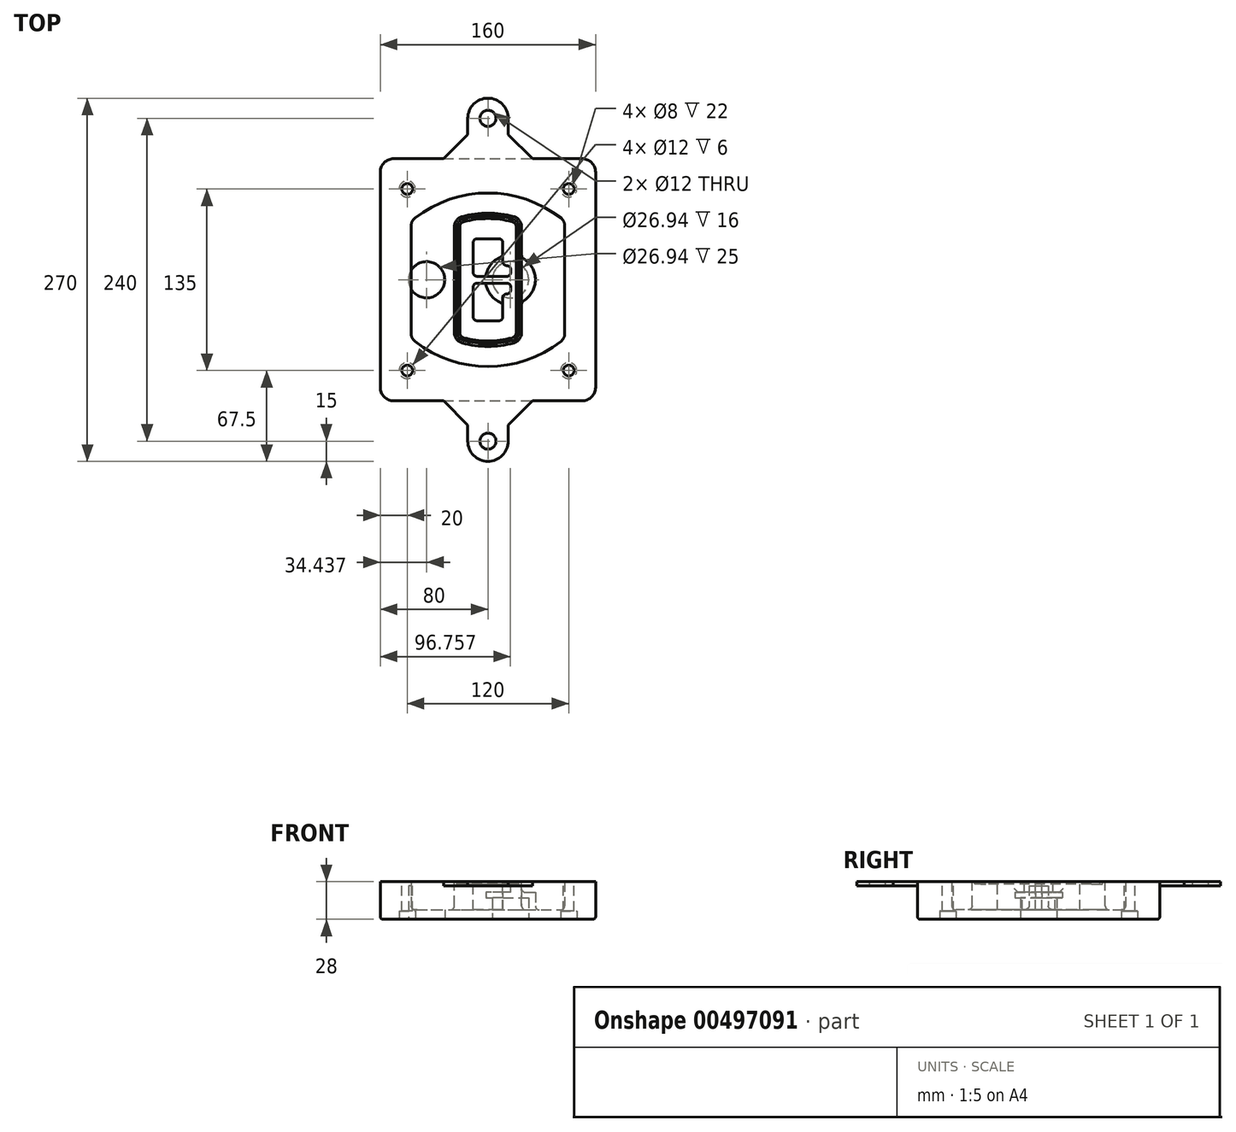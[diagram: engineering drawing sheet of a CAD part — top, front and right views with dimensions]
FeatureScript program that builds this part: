
annotation { "Feature Type Name" : "Feature", "Feature Type Description" : "" }
export const myFeature = defineFeature(function(context is Context, id is Id, definition is map)
    precondition{}
    {
        {
            var Q0;
            Q0=qCreatedBy(makeId("Top.planeOp"),FACE);
            var sketch = newSketch(context, id + "F0", { "sketchPlane" : qUnion([Q0])});
            skPoint(sketch, "E0.rect.middle", {"position": v(0, 0) * mm});
            skLineSegment(sketch, "E1.bottom", {"start": v(-70, -90) * mm, "end": v(70, -90) * mm});
            skLineSegment(sketch, "E1.top", {"start": v(-70, 90) * mm, "end": v(70, 90) * mm});
            skLineSegment(sketch, "E1.left", {"start": v(-80, -80) * mm, "end": v(-80, 80) * mm});
            skLineSegment(sketch, "E1.right", {"start": v(80, -80) * mm, "end": v(80, 80) * mm});
            skLineSegment(sketch, "E2", {"start": v(-80, 90) * mm, "end": v(80, -90) * mm, "construction": true});
            skLineSegment(sketch, "E3", {"start": v(80, 90) * mm, "end": v(-80, -90) * mm, "construction": true});
            skCircle(sketch, "E4", {"center": v(-60, 67.5) * mm, "radius": 4 * mm});
            skCircle(sketch, "E5", {"center": v(60, 67.5) * mm, "radius": 4 * mm});
            skCircle(sketch, "E6", {"center": v(60, -67.5) * mm, "radius": 4 * mm});
            skCircle(sketch, "E7", {"center": v(-60, -67.5) * mm, "radius": 4 * mm});
            skLineSegment(sketch, "E8", {"start": v(-60, 67.5) * mm, "end": v(60, 67.5) * mm, "construction": true});
            skLineSegment(sketch, "E9", {"start": v(60, 67.5) * mm, "end": v(60, -67.5) * mm, "construction": true});
            skLineSegment(sketch, "E10", {"start": v(60, -67.5) * mm, "end": v(-60, -67.5) * mm, "construction": true});
            skLineSegment(sketch, "E11", {"start": v(-60, -67.5) * mm, "end": v(-60, 67.5) * mm, "construction": true});
            skLineSegment(sketch, "E12", {"start": v(-60, 40.3) * mm, "end": v(-60, -40.3) * mm});
            skLineSegment(sketch, "E13", {"start": v(60, 40.3) * mm, "end": v(60, -40.3) * mm});
            skArc(sketch, "E14", {"start": v(56.15, 48.18) * mm, "mid": v(0, 67.5) * mm, "end": v(-56.15, 48.18) * mm});
            skArc(sketch, "E15", {"start": v(-56.15, -48.18) * mm, "mid": v(0, -67.5) * mm, "end": v(56.15, -48.18) * mm});
            skLineSegment(sketch, "E16", {"start": v(-60, 0) * mm, "end": v(60, 0) * mm, "construction": true});
            skPoint(sketch, "E17.visualSharp", {"position": v(-60, -45) * mm});
            skArc(sketch, "E17.filletArc", {"start": v(-60, -40.3) * mm, "mid": v(-58.99, -44.68) * mm, "end": v(-56.15, -48.18) * mm});
            skPoint(sketch, "E18.visualSharp", {"position": v(-60, 45) * mm});
            skArc(sketch, "E18.filletArc", {"start": v(-56.15, 48.18) * mm, "mid": v(-58.99, 44.68) * mm, "end": v(-60, 40.3) * mm});
            skPoint(sketch, "E19.visualSharp", {"position": v(60, 45) * mm});
            skArc(sketch, "E19.filletArc", {"start": v(60, 40.3) * mm, "mid": v(58.99, 44.68) * mm, "end": v(56.15, 48.18) * mm});
            skPoint(sketch, "E20.visualSharp", {"position": v(60, -45) * mm});
            skArc(sketch, "E20.filletArc", {"start": v(56.15, -48.18) * mm, "mid": v(58.99, -44.68) * mm, "end": v(60, -40.3) * mm});
            skPoint(sketch, "E21.visualSharp", {"position": v(-80, 90) * mm});
            skArc(sketch, "E21.filletArc", {"start": v(-70, 90) * mm, "mid": v(-77.07, 87.07) * mm, "end": v(-80, 80) * mm});
            skPoint(sketch, "E22.visualSharp", {"position": v(80, 90) * mm});
            skArc(sketch, "E22.filletArc", {"start": v(80, 80) * mm, "mid": v(77.07, 87.07) * mm, "end": v(70, 90) * mm});
            skPoint(sketch, "E23.visualSharp", {"position": v(80, -90) * mm});
            skArc(sketch, "E23.filletArc", {"start": v(70, -90) * mm, "mid": v(77.07, -87.07) * mm, "end": v(80, -80) * mm});
            skPoint(sketch, "E24.visualSharp", {"position": v(-80, -90) * mm});
            skArc(sketch, "E24.filletArc", {"start": v(-80, -80) * mm, "mid": v(-77.07, -87.07) * mm, "end": v(-70, -90) * mm});
            skArc(sketch, "E25.0", {"start": v(57, 40.3) * mm, "mid": v(56.3, 43.36) * mm, "end": v(54.3, 45.81) * mm});
            skLineSegment(sketch, "E25.1", {"start": v(57, 40.3) * mm, "end": v(57, -40.3) * mm});
            skArc(sketch, "E25.2", {"start": v(54.3, -45.81) * mm, "mid": v(56.3, -43.36) * mm, "end": v(57, -40.3) * mm});
            skArc(sketch, "E25.3", {"start": v(-54.3, -45.81) * mm, "mid": v(0, -64.5) * mm, "end": v(54.3, -45.81) * mm});
            skArc(sketch, "E25.4", {"start": v(-57, -40.3) * mm, "mid": v(-56.3, -43.36) * mm, "end": v(-54.3, -45.81) * mm});
            skArc(sketch, "E25.5", {"start": v(54.3, 45.81) * mm, "mid": v(0, 64.5) * mm, "end": v(-54.3, 45.81) * mm});
            skLineSegment(sketch, "E25.6", {"start": v(-57, 40.3) * mm, "end": v(-57, -40.3) * mm});
            skArc(sketch, "E25.7", {"start": v(-54.3, 45.81) * mm, "mid": v(-56.3, 43.36) * mm, "end": v(-57, 40.3) * mm});
            skArc(sketch, "E26.0", {"start": v(-58.62, 51.33) * mm, "mid": v(-62.58, 46.43) * mm, "end": v(-64, 40.3) * mm});
            skArc(sketch, "E26.1", {"start": v(58.62, 51.33) * mm, "mid": v(0, 71.5) * mm, "end": v(-58.62, 51.33) * mm});
            skArc(sketch, "E26.2", {"start": v(64, 40.3) * mm, "mid": v(62.58, 46.43) * mm, "end": v(58.62, 51.33) * mm});
            skLineSegment(sketch, "E26.3", {"start": v(64, 40.3) * mm, "end": v(64, -40.3) * mm});
            skArc(sketch, "E26.4", {"start": v(58.62, -51.33) * mm, "mid": v(62.58, -46.43) * mm, "end": v(64, -40.3) * mm});
            skLineSegment(sketch, "E26.5", {"start": v(-64, 40.3) * mm, "end": v(-64, -40.3) * mm});
            skArc(sketch, "E26.6", {"start": v(-58.62, -51.33) * mm, "mid": v(0, -71.5) * mm, "end": v(58.62, -51.33) * mm});
            skArc(sketch, "E26.7", {"start": v(-64, -40.3) * mm, "mid": v(-62.58, -46.43) * mm, "end": v(-58.62, -51.33) * mm});
            skSolve(sketch);
        }
        {
            var Q0;
            Q0=makeQuery(id+"F0.imprint","IMPRINT",FACE,{"disambiguationData":[TD([[makeQuery(id+"F0.imprint","IMPRINT",EDGE,{"derivedFrom":sQuery(id+"F0.wireOp",EDGE,"E1.bottom")}),1.0]])]});
            var Q1;
            Q1=makeQuery(id+"F0.imprint","IMPRINT",FACE,{"disambiguationData":[TD([[makeQuery(id+"F0.imprint","IMPRINT",EDGE,{"derivedFrom":sQuery(id+"F0.wireOp",EDGE,"E12")}),1.0]])]});
            var Q2;
            Q2=makeQuery(id+"F0.imprint","IMPRINT",FACE,{"disambiguationData":[TD([[makeQuery(id+"F0.imprint","IMPRINT",EDGE,{"derivedFrom":sQuery(id+"F0.wireOp",EDGE,"E25.0")}),1.0]])]});
            var Q3;
            Q3=makeQuery(id+"F0.imprint","IMPRINT",FACE,{"disambiguationData":[TD([[makeQuery(id+"F0.imprint","IMPRINT",EDGE,{"derivedFrom":sQuery(id+"F0.wireOp",EDGE,"E12")}),-1.0]])]});
            extrude(context, id + "F1", {"entities" : qUnion([Q0, Q1, Q2, Q3]), "oppositeDirection" : true, "depth" : 25 * mm});
        }
        {
            var Q0;
            Q0=makeQuery(id+"F0.imprint","IMPRINT",FACE,{"disambiguationData":[TD([[makeQuery(id+"F0.imprint","IMPRINT",EDGE,{"derivedFrom":sQuery(id+"F0.wireOp",EDGE,"E12")}),1.0]])]});
            extrude(context, id + "F2", {"entities" : qUnion([Q0]), "operationType" : NewBodyOperationType.ADD, "depth" : 3 * mm});
        }
        {
            var Q0;
            Q0=makeQuery(id+"F0.imprint","IMPRINT",FACE,{"disambiguationData":[TD([[makeQuery(id+"F0.imprint","IMPRINT",EDGE,{"derivedFrom":sQuery(id+"F0.wireOp",EDGE,"E25.0")}),1.0]])]});
            extrude(context, id + "F3", {"entities" : qUnion([Q0]), "operationType" : NewBodyOperationType.REMOVE, "oppositeDirection" : true, "depth" : 18 * mm});
        }
        {
            var Q0;
            Q0=makeQuery(id+"F2.opExtrude","CAP_FACE",FACE,{"disambiguationData":[OSD([sQuery(id+"F0.wireOp",EDGE,"E12"),sQuery(id+"F0.wireOp",EDGE,"E13"),sQuery(id+"F0.wireOp",EDGE,"E14"),sQuery(id+"F0.wireOp",EDGE,"E15"),sQuery(id+"F0.wireOp",EDGE,"E17.filletArc"),sQuery(id+"F0.wireOp",EDGE,"E18.filletArc"),sQuery(id+"F0.wireOp",EDGE,"E19.filletArc"),sQuery(id+"F0.wireOp",EDGE,"E20.filletArc"),sQuery(id+"F0.wireOp",EDGE,"E25.0"),sQuery(id+"F0.wireOp",EDGE,"E25.1"),sQuery(id+"F0.wireOp",EDGE,"E25.2"),sQuery(id+"F0.wireOp",EDGE,"E25.3"),sQuery(id+"F0.wireOp",EDGE,"E25.4"),sQuery(id+"F0.wireOp",EDGE,"E25.5"),sQuery(id+"F0.wireOp",EDGE,"E25.6"),sQuery(id+"F0.wireOp",EDGE,"E25.7")])],"isStart":false});
            var sketch = newSketch(context, id + "F4", { "sketchPlane" : qUnion([Q0])});
            skArc(sketch, "E27.0", {"start": v(-19.08, -46.97) * mm, "mid": v(0, -49.5) * mm, "end": v(19.08, -46.97) * mm});
            skArc(sketch, "E28.0", {"start": v(19.08, 46.97) * mm, "mid": v(0, 49.5) * mm, "end": v(-19.08, 46.97) * mm});
            skLineSegment(sketch, "E29", {"start": v(-25, 39.25) * mm, "end": v(-25, -39.25) * mm});
            skLineSegment(sketch, "E30", {"start": v(25, 39.25) * mm, "end": v(25, -39.25) * mm});
            skLineSegment(sketch, "E31", {"start": v(-25, 45.1) * mm, "end": v(25, 45.1) * mm, "construction": true});
            skLineSegment(sketch, "E32", {"start": v(-25, -45.1) * mm, "end": v(25, -45.1) * mm, "construction": true});
            skPoint(sketch, "E33.visualSharp", {"position": v(-25, 45.1) * mm});
            skArc(sketch, "E33.filletArc", {"start": v(-19.08, 46.97) * mm, "mid": v(-23.35, 44.11) * mm, "end": v(-25, 39.25) * mm});
            skPoint(sketch, "E34.visualSharp", {"position": v(25, 45.1) * mm});
            skArc(sketch, "E34.filletArc", {"start": v(25, 39.25) * mm, "mid": v(23.35, 44.11) * mm, "end": v(19.08, 46.97) * mm});
            skPoint(sketch, "E35.visualSharp", {"position": v(25, -45.1) * mm});
            skArc(sketch, "E35.filletArc", {"start": v(19.08, -46.97) * mm, "mid": v(23.35, -44.11) * mm, "end": v(25, -39.25) * mm});
            skPoint(sketch, "E36.visualSharp", {"position": v(-25, -45.1) * mm});
            skArc(sketch, "E36.filletArc", {"start": v(-25, -39.25) * mm, "mid": v(-23.35, -44.11) * mm, "end": v(-19.08, -46.97) * mm});
            skArc(sketch, "E37.0", {"start": v(54.3, 45.81) * mm, "mid": v(0, 64.5) * mm, "end": v(-54.3, 45.81) * mm});
            skArc(sketch, "E37.1", {"start": v(-54.3, 45.81) * mm, "mid": v(-56.3, 43.36) * mm, "end": v(-57, 40.3) * mm});
            skLineSegment(sketch, "E37.2", {"start": v(-57, 40.3) * mm, "end": v(-57, -40.3) * mm});
            skArc(sketch, "E37.3", {"start": v(-57, -40.3) * mm, "mid": v(-56.3, -43.36) * mm, "end": v(-54.3, -45.81) * mm});
            skArc(sketch, "E37.4", {"start": v(-54.3, -45.81) * mm, "mid": v(0, -64.5) * mm, "end": v(54.3, -45.81) * mm});
            skArc(sketch, "E37.5", {"start": v(54.3, -45.81) * mm, "mid": v(56.3, -43.36) * mm, "end": v(57, -40.3) * mm});
            skLineSegment(sketch, "E37.6", {"start": v(57, 40.3) * mm, "end": v(57, -40.3) * mm});
            skArc(sketch, "E37.7", {"start": v(57, 40.3) * mm, "mid": v(56.3, 43.36) * mm, "end": v(54.3, 45.81) * mm});
            skLineSegment(sketch, "E38.0", {"start": v(23, 39.25) * mm, "end": v(23, -39.25) * mm});
            skArc(sketch, "E38.1", {"start": v(18.56, -45.04) * mm, "mid": v(21.76, -42.9) * mm, "end": v(23, -39.25) * mm});
            skArc(sketch, "E38.2", {"start": v(-18.56, -45.04) * mm, "mid": v(0, -47.5) * mm, "end": v(18.56, -45.04) * mm});
            skArc(sketch, "E38.3", {"start": v(-23, -39.25) * mm, "mid": v(-21.76, -42.9) * mm, "end": v(-18.56, -45.04) * mm});
            skLineSegment(sketch, "E38.4", {"start": v(-23, 39.25) * mm, "end": v(-23, -39.25) * mm});
            skArc(sketch, "E38.5", {"start": v(23, 39.25) * mm, "mid": v(21.76, 42.9) * mm, "end": v(18.56, 45.04) * mm});
            skArc(sketch, "E38.6", {"start": v(-18.56, 45.04) * mm, "mid": v(-21.76, 42.9) * mm, "end": v(-23, 39.25) * mm});
            skArc(sketch, "E38.7", {"start": v(18.56, 45.04) * mm, "mid": v(0, 47.5) * mm, "end": v(-18.56, 45.04) * mm});
            skArc(sketch, "E39.0", {"start": v(21, 39.25) * mm, "mid": v(20.18, 41.68) * mm, "end": v(18.04, 43.1) * mm});
            skLineSegment(sketch, "E39.1", {"start": v(21, 39.25) * mm, "end": v(21, -39.25) * mm});
            skArc(sketch, "E39.2", {"start": v(18.04, -43.1) * mm, "mid": v(20.18, -41.68) * mm, "end": v(21, -39.25) * mm});
            skArc(sketch, "E39.3", {"start": v(-18.04, -43.1) * mm, "mid": v(0, -45.5) * mm, "end": v(18.04, -43.1) * mm});
            skArc(sketch, "E39.4", {"start": v(-21, -39.25) * mm, "mid": v(-20.18, -41.68) * mm, "end": v(-18.04, -43.1) * mm});
            skArc(sketch, "E39.5", {"start": v(18.04, 43.1) * mm, "mid": v(0, 45.5) * mm, "end": v(-18.04, 43.1) * mm});
            skLineSegment(sketch, "E39.6", {"start": v(-21, 39.25) * mm, "end": v(-21, -39.25) * mm});
            skArc(sketch, "E39.7", {"start": v(-18.04, 43.1) * mm, "mid": v(-20.18, 41.68) * mm, "end": v(-21, 39.25) * mm});
            skLineSegment(sketch, "E40", {"start": v(-25, 0) * mm, "end": v(25, 0) * mm, "construction": true});
            skLineSegment(sketch, "E41", {"start": v(-11, 5.5) * mm, "end": v(-11, 27.5) * mm});
            skLineSegment(sketch, "E42", {"start": v(-8, 30.5) * mm, "end": v(8, 30.5) * mm});
            skLineSegment(sketch, "E43", {"start": v(11, 27.5) * mm, "end": v(11, 13.5) * mm});
            skLineSegment(sketch, "E44", {"start": v(14, 10.5) * mm, "end": v(14, 10.5) * mm});
            skLineSegment(sketch, "E45", {"start": v(17, 7.5) * mm, "end": v(17, 5.5) * mm});
            skLineSegment(sketch, "E46", {"start": v(14, 2.5) * mm, "end": v(-8, 2.5) * mm});
            skPoint(sketch, "E47.visualSharp", {"position": v(-11, 30.5) * mm});
            skArc(sketch, "E47.filletArc", {"start": v(-8, 30.5) * mm, "mid": v(-10.12, 29.62) * mm, "end": v(-11, 27.5) * mm});
            skPoint(sketch, "E48.visualSharp", {"position": v(11, 30.5) * mm});
            skArc(sketch, "E48.filletArc", {"start": v(11, 27.5) * mm, "mid": v(10.12, 29.62) * mm, "end": v(8, 30.5) * mm});
            skPoint(sketch, "E49.visualSharp", {"position": v(11, 10.5) * mm});
            skArc(sketch, "E49.filletArc", {"start": v(11, 13.5) * mm, "mid": v(11.88, 11.38) * mm, "end": v(14, 10.5) * mm});
            skPoint(sketch, "E50.visualSharp", {"position": v(17, 10.5) * mm});
            skArc(sketch, "E50.filletArc", {"start": v(17, 7.5) * mm, "mid": v(16.12, 9.62) * mm, "end": v(14, 10.5) * mm});
            skPoint(sketch, "E51.visualSharp", {"position": v(17, 2.5) * mm});
            skArc(sketch, "E51.filletArc", {"start": v(14, 2.5) * mm, "mid": v(16.12, 3.38) * mm, "end": v(17, 5.5) * mm});
            skPoint(sketch, "E52.visualSharp", {"position": v(-11, 2.5) * mm});
            skArc(sketch, "E52.filletArc", {"start": v(-11, 5.5) * mm, "mid": v(-10.12, 3.38) * mm, "end": v(-8, 2.5) * mm});
            skLineSegment(sketch, "E53.0.MirrorCS", {"start": v(14, -2.5) * mm, "end": v(-8, -2.5) * mm});
            skArc(sketch, "E54.0.MirrorCS", {"start": v(-11, -5.5) * mm, "mid": v(-10.12, -3.38) * mm, "end": v(-8, -2.5) * mm});
            skLineSegment(sketch, "E55.0.MirrorCS", {"start": v(-11, -5.5) * mm, "end": v(-11, -27.5) * mm});
            skArc(sketch, "E56.0.MirrorCS", {"start": v(-8, -30.5) * mm, "mid": v(-10.12, -29.62) * mm, "end": v(-11, -27.5) * mm});
            skLineSegment(sketch, "E57.0.MirrorCS", {"start": v(-8, -30.5) * mm, "end": v(8, -30.5) * mm});
            skArc(sketch, "E58.0.MirrorCS", {"start": v(11, -27.5) * mm, "mid": v(10.12, -29.62) * mm, "end": v(8, -30.5) * mm});
            skLineSegment(sketch, "E59.0.MirrorCS", {"start": v(11, -27.5) * mm, "end": v(11, -13.5) * mm});
            skArc(sketch, "E60.0.MirrorCS", {"start": v(11, -13.5) * mm, "mid": v(11.88, -11.38) * mm, "end": v(14, -10.5) * mm});
            skArc(sketch, "E61.0.MirrorCS", {"start": v(17, -7.5) * mm, "mid": v(16.12, -9.62) * mm, "end": v(14, -10.5) * mm});
            skLineSegment(sketch, "E62.0.MirrorCS", {"start": v(17, -7.5) * mm, "end": v(17, -5.5) * mm});
            skArc(sketch, "E63.0.MirrorCS", {"start": v(14, -2.5) * mm, "mid": v(16.12, -3.38) * mm, "end": v(17, -5.5) * mm});
            skSolve(sketch);
        }
        {
            var Q0;
            Q0=makeQuery(id+"F4.imprint","IMPRINT",FACE,{"disambiguationData":[TD([[makeQuery(id+"F4.imprint","IMPRINT",EDGE,{"derivedFrom":sQuery(id+"F4.wireOp",EDGE,"E27.0")}),1.0]])]});
            var Q1;
            Q1=makeQuery(id+"F4.imprint","IMPRINT",FACE,{"disambiguationData":[TD([[makeQuery(id+"F4.imprint","IMPRINT",EDGE,{"derivedFrom":sQuery(id+"F4.wireOp",EDGE,"E38.0")}),-1.0]])]});
            var Q2;
            Q2=makeQuery(id+"F4.imprint","IMPRINT",FACE,{"disambiguationData":[TD([[makeQuery(id+"F4.imprint","IMPRINT",EDGE,{"derivedFrom":sQuery(id+"F4.wireOp",EDGE,"E39.0")}),1.0]])]});
            extrude(context, id + "F5", {"entities" : qUnion([Q0, Q1, Q2]), "operationType" : NewBodyOperationType.ADD, "endBound" : BoundingType.UP_TO_NEXT, "oppositeDirection" : true, "depth" : 25 * mm});
        }
        {
            var Q0;
            Q0=makeQuery(id+"F4.imprint","IMPRINT",FACE,{"disambiguationData":[TD([[makeQuery(id+"F4.imprint","IMPRINT",EDGE,{"derivedFrom":sQuery(id+"F4.wireOp",EDGE,"E38.0")}),-1.0]])]});
            extrude(context, id + "F6", {"entities" : qUnion([Q0]), "operationType" : NewBodyOperationType.REMOVE, "oppositeDirection" : true, "depth" : 2 * mm});
        }
        {
            var Q0;
            Q0=makeQuery(id+"F1.opExtrude","CAP_FACE",FACE,{"disambiguationData":[OSD([sQuery(id+"F0.wireOp",EDGE,"E1.bottom"),sQuery(id+"F0.wireOp",EDGE,"E1.top"),sQuery(id+"F0.wireOp",EDGE,"E1.left"),sQuery(id+"F0.wireOp",EDGE,"E1.right"),sQuery(id+"F0.wireOp",EDGE,"E4"),sQuery(id+"F0.wireOp",EDGE,"E5"),sQuery(id+"F0.wireOp",EDGE,"E6"),sQuery(id+"F0.wireOp",EDGE,"E7"),sQuery(id+"F0.wireOp",EDGE,"E21.filletArc"),sQuery(id+"F0.wireOp",EDGE,"E22.filletArc"),sQuery(id+"F0.wireOp",EDGE,"E23.filletArc"),sQuery(id+"F0.wireOp",EDGE,"E24.filletArc")])],"isStart":false});
            var sketch = newSketch(context, id + "F7", { "sketchPlane" : qUnion([Q0])});
            skCircle(sketch, "E64", {"center": v(16.76, 0) * mm, "radius": 13.47 * mm});
            skCircle(sketch, "E65", {"center": v(-45.56, 0) * mm, "radius": 13.47 * mm});
            skLineSegment(sketch, "E66", {"start": v(80, 0) * mm, "end": v(-80, 0) * mm});
            skCircle(sketch, "E67", {"center": v(16.76, 0) * mm, "radius": 18.47 * mm});
            skCircle(sketch, "E68", {"center": v(60, -67.5) * mm, "radius": 6 * mm});
            skCircle(sketch, "E69", {"center": v(-60, -67.5) * mm, "radius": 6 * mm});
            skCircle(sketch, "E70", {"center": v(-60, 67.5) * mm, "radius": 6 * mm});
            skCircle(sketch, "E71", {"center": v(60, 67.5) * mm, "radius": 6 * mm});
            skSolve(sketch);
        }
        {
            var Q0;
            {var subQ1=sQuery(id+"F7.wireOp",EDGE,"E66");var subQ4=sQuery(id+"F7.wireOp",EDGE,"E64");var subQ6=makeQuery(id+"F7.imprint","INTERSECT",VERTEX,{"disambiguationData":[OD(0.0)],"derivedFrom":[subQ4,subQ1]});Q0=makeQuery(id+"F7.imprint","IMPRINT",FACE,{"disambiguationData":[TD([[makeQuery(id+"F7.imprint","IMPRINT",EDGE,{"disambiguationData":[TD([[subQ6,-1.0]])],"derivedFrom":subQ4}),-1.0]])]});}
            var Q1;
            {var subQ0=sQuery(id+"F7.wireOp",EDGE,"E66");var subQ1=sQuery(id+"F7.wireOp",EDGE,"E64");var subQ3=makeQuery(id+"F7.imprint","INTERSECT",VERTEX,{"disambiguationData":[OD(0.0)],"derivedFrom":[subQ1,subQ0]});Q1=makeQuery(id+"F7.imprint","IMPRINT",FACE,{"disambiguationData":[TD([[makeQuery(id+"F7.imprint","IMPRINT",EDGE,{"disambiguationData":[TD([[subQ3,-1.0]])],"derivedFrom":subQ1}),1.0]])]});}
            var Q2;
            {var subQ0=sQuery(id+"F7.wireOp",EDGE,"E66");var subQ1=sQuery(id+"F7.wireOp",EDGE,"E64");var subQ3=makeQuery(id+"F7.imprint","INTERSECT",VERTEX,{"disambiguationData":[OD(0.0)],"derivedFrom":[subQ1,subQ0]});Q2=makeQuery(id+"F7.imprint","IMPRINT",FACE,{"disambiguationData":[TD([[makeQuery(id+"F7.imprint","IMPRINT",EDGE,{"disambiguationData":[TD([[subQ3,1.0]])],"derivedFrom":subQ1}),1.0]])]});}
            var Q3;
            {var subQ1=sQuery(id+"F7.wireOp",EDGE,"E66");var subQ4=sQuery(id+"F7.wireOp",EDGE,"E64");var subQ6=makeQuery(id+"F7.imprint","INTERSECT",VERTEX,{"disambiguationData":[OD(0.0)],"derivedFrom":[subQ4,subQ1]});Q3=makeQuery(id+"F7.imprint","IMPRINT",FACE,{"disambiguationData":[TD([[makeQuery(id+"F7.imprint","IMPRINT",EDGE,{"disambiguationData":[TD([[subQ6,1.0]])],"derivedFrom":subQ4}),-1.0]])]});}
            extrude(context, id + "F8", {"entities" : qUnion([Q0, Q1, Q2, Q3]), "operationType" : NewBodyOperationType.ADD, "oppositeDirection" : true, "depth" : 20 * mm});
        }
        {
            var Q0;
            {var subQ0=sQuery(id+"F7.wireOp",EDGE,"E66");var subQ1=sQuery(id+"F7.wireOp",EDGE,"E64");var subQ3=makeQuery(id+"F7.imprint","INTERSECT",VERTEX,{"disambiguationData":[OD(0.0)],"derivedFrom":[subQ1,subQ0]});Q0=makeQuery(id+"F7.imprint","IMPRINT",FACE,{"disambiguationData":[TD([[makeQuery(id+"F7.imprint","IMPRINT",EDGE,{"disambiguationData":[TD([[subQ3,-1.0]])],"derivedFrom":subQ1}),1.0]])]});}
            var Q1;
            {var subQ0=sQuery(id+"F7.wireOp",EDGE,"E66");var subQ1=sQuery(id+"F7.wireOp",EDGE,"E64");var subQ3=makeQuery(id+"F7.imprint","INTERSECT",VERTEX,{"disambiguationData":[OD(0.0)],"derivedFrom":[subQ1,subQ0]});Q1=makeQuery(id+"F7.imprint","IMPRINT",FACE,{"disambiguationData":[TD([[makeQuery(id+"F7.imprint","IMPRINT",EDGE,{"disambiguationData":[TD([[subQ3,1.0]])],"derivedFrom":subQ1}),1.0]])]});}
            extrude(context, id + "F9", {"entities" : qUnion([Q0, Q1]), "operationType" : NewBodyOperationType.REMOVE, "oppositeDirection" : true, "depth" : 16 * mm});
        }
        {
            var Q0;
            {var subQ0=sQuery(id+"F7.wireOp",EDGE,"E66");var subQ1=sQuery(id+"F7.wireOp",EDGE,"E65");var subQ3=makeQuery(id+"F7.imprint","INTERSECT",VERTEX,{"disambiguationData":[OD(0.0)],"derivedFrom":[subQ1,subQ0]});Q0=makeQuery(id+"F7.imprint","IMPRINT",FACE,{"disambiguationData":[TD([[makeQuery(id+"F7.imprint","IMPRINT",EDGE,{"disambiguationData":[TD([[subQ3,-1.0]])],"derivedFrom":subQ1}),1.0]])]});}
            var Q1;
            {var subQ0=sQuery(id+"F7.wireOp",EDGE,"E66");var subQ1=sQuery(id+"F7.wireOp",EDGE,"E65");var subQ3=makeQuery(id+"F7.imprint","INTERSECT",VERTEX,{"disambiguationData":[OD(0.0)],"derivedFrom":[subQ1,subQ0]});Q1=makeQuery(id+"F7.imprint","IMPRINT",FACE,{"disambiguationData":[TD([[makeQuery(id+"F7.imprint","IMPRINT",EDGE,{"disambiguationData":[TD([[subQ3,1.0]])],"derivedFrom":subQ1}),1.0]])]});}
            extrude(context, id + "F10", {"entities" : qUnion([Q0, Q1]), "operationType" : NewBodyOperationType.REMOVE, "oppositeDirection" : true, "depth" : 25 * mm});
        }
        {
            var Q0;
            Q0=makeQuery(id+"F7.imprint","IMPRINT",FACE,{"disambiguationData":[TD([[makeQuery(id+"F7.imprint","IMPRINT",EDGE,{"derivedFrom":sQuery(id+"F7.wireOp",EDGE,"E68")}),1.0]])]});
            var Q1;
            Q1=makeQuery(id+"F7.imprint","IMPRINT",FACE,{"disambiguationData":[TD([[makeQuery(id+"F7.imprint","IMPRINT",EDGE,{"derivedFrom":makeQuery(id+"F1.opExtrude","CAP_EDGE",EDGE,{"disambiguationData":[OSD([sQuery(id+"F0.wireOp",EDGE,"E5")])],"isStart":false})}),-1.0]])]});
            var Q2;
            Q2=makeQuery(id+"F7.imprint","IMPRINT",FACE,{"disambiguationData":[TD([[makeQuery(id+"F7.imprint","IMPRINT",EDGE,{"derivedFrom":sQuery(id+"F7.wireOp",EDGE,"E69")}),1.0]])]});
            var Q3;
            Q3=makeQuery(id+"F7.imprint","IMPRINT",FACE,{"disambiguationData":[TD([[makeQuery(id+"F7.imprint","IMPRINT",EDGE,{"derivedFrom":makeQuery(id+"F1.opExtrude","CAP_EDGE",EDGE,{"disambiguationData":[OSD([sQuery(id+"F0.wireOp",EDGE,"E4")])],"isStart":false})}),-1.0]])]});
            var Q4;
            Q4=makeQuery(id+"F7.imprint","IMPRINT",FACE,{"disambiguationData":[TD([[makeQuery(id+"F7.imprint","IMPRINT",EDGE,{"derivedFrom":sQuery(id+"F7.wireOp",EDGE,"E70")}),1.0]])]});
            var Q5;
            Q5=makeQuery(id+"F7.imprint","IMPRINT",FACE,{"disambiguationData":[TD([[makeQuery(id+"F7.imprint","IMPRINT",EDGE,{"derivedFrom":makeQuery(id+"F1.opExtrude","CAP_EDGE",EDGE,{"disambiguationData":[OSD([sQuery(id+"F0.wireOp",EDGE,"E7")])],"isStart":false})}),-1.0]])]});
            var Q6;
            Q6=makeQuery(id+"F7.imprint","IMPRINT",FACE,{"disambiguationData":[TD([[makeQuery(id+"F7.imprint","IMPRINT",EDGE,{"derivedFrom":sQuery(id+"F7.wireOp",EDGE,"E71")}),1.0]])]});
            var Q7;
            Q7=makeQuery(id+"F7.imprint","IMPRINT",FACE,{"disambiguationData":[TD([[makeQuery(id+"F7.imprint","IMPRINT",EDGE,{"derivedFrom":makeQuery(id+"F1.opExtrude","CAP_EDGE",EDGE,{"disambiguationData":[OSD([sQuery(id+"F0.wireOp",EDGE,"E6")])],"isStart":false})}),-1.0]])]});
            extrude(context, id + "F11", {"entities" : qUnion([Q0, Q1, Q2, Q3, Q4, Q5, Q6, Q7]), "operationType" : NewBodyOperationType.REMOVE, "oppositeDirection" : true, "depth" : 6 * mm});
        }
        {
            var Q0;
            Q0=makeQuery(id+"F9.boolean.opBoolean","COPY",FACE,{"derivedFrom":makeQuery(id+"F9.opExtrude","CAP_FACE",FACE,{"disambiguationData":[OSD([sQuery(id+"F7.wireOp",EDGE,"E64")])],"isStart":false})});
            var sketch = newSketch(context, id + "F12", { "sketchPlane" : qUnion([Q0])});
            skArc(sketch, "E72.0", {"start": v(11, 17.55) * mm, "mid": v(2.57, 11.82) * mm, "end": v(-1.54, 2.5) * mm});
            skArc(sketch, "E72.1", {"start": v(-1.54, -2.5) * mm, "mid": v(2.57, -11.82) * mm, "end": v(11, -17.55) * mm});
            skLineSegment(sketch, "E73", {"start": v(-1.54, -2.5) * mm, "end": v(14, -2.5) * mm});
            skLineSegment(sketch, "E74.0", {"start": v(14, 2.5) * mm, "end": v(-1.54, 2.5) * mm});
            skArc(sketch, "E74.1", {"start": v(14, 2.5) * mm, "mid": v(16.12, 3.38) * mm, "end": v(17, 5.5) * mm});
            skLineSegment(sketch, "E74.2", {"start": v(17, 7.5) * mm, "end": v(17, 5.5) * mm});
            skArc(sketch, "E74.3", {"start": v(17, 7.5) * mm, "mid": v(16.12, 9.62) * mm, "end": v(14, 10.5) * mm});
            skArc(sketch, "E74.4", {"start": v(11, 13.5) * mm, "mid": v(11.88, 11.38) * mm, "end": v(14, 10.5) * mm});
            skLineSegment(sketch, "E74.5", {"start": v(11, 17.55) * mm, "end": v(11, 13.5) * mm});
            skLineSegment(sketch, "E74.7", {"start": v(14, -2.5) * mm, "end": v(-1.54, -2.5) * mm});
            skArc(sketch, "E74.8", {"start": v(14, -2.5) * mm, "mid": v(16.12, -3.38) * mm, "end": v(17, -5.5) * mm});
            skLineSegment(sketch, "E74.9", {"start": v(17, -7.5) * mm, "end": v(17, -5.5) * mm});
            skArc(sketch, "E74.10", {"start": v(17, -7.5) * mm, "mid": v(16.12, -9.62) * mm, "end": v(14, -10.5) * mm});
            skArc(sketch, "E74.11", {"start": v(11, -13.5) * mm, "mid": v(11.88, -11.38) * mm, "end": v(14, -10.5) * mm});
            skLineSegment(sketch, "E74.12", {"start": v(11, -17.55) * mm, "end": v(11, -13.5) * mm});
            skPoint(sketch, "E75.orphan", {"position": v(11, -27.5) * mm});
            skPoint(sketch, "E76.orphan", {"position": v(-8, -2.5) * mm});
            skPoint(sketch, "E77.orphan", {"position": v(-8, 2.5) * mm});
            skPoint(sketch, "E78.orphan", {"position": v(11, 27.5) * mm});
            skSolve(sketch);
        }
        {
            var Q0;
            {var subQ7=sQuery(id+"F12.wireOp",EDGE,"E72.0");var subQ14=sQuery(id+"F12.wireOp",EDGE,"E72.1");var subQ16=sQuery(id+"F12.wireOp",EDGE,"E74.1");var subQ18=sQuery(id+"F12.wireOp",EDGE,"E74.8");Q0=qUnion([makeQuery(id+"F12.imprint","IMPRINT",FACE,{"disambiguationData":[TD([[makeQuery(id+"F12.imprint","IMPRINT",EDGE,{"derivedFrom":subQ7}),1.0]])]}),makeQuery(id+"F12.imprint","IMPRINT",FACE,{"disambiguationData":[TD([[makeQuery(id+"F12.imprint","IMPRINT",EDGE,{"derivedFrom":subQ14}),1.0]])]}),makeQuery(id+"F12.imprint","IMPRINT",FACE,{"disambiguationData":[TD([[makeQuery(id+"F12.imprint","IMPRINT",EDGE,{"derivedFrom":subQ16}),1.0]])]}),makeQuery(id+"F12.imprint","IMPRINT",FACE,{"disambiguationData":[TD([[makeQuery(id+"F12.imprint","IMPRINT",EDGE,{"derivedFrom":subQ18}),-1.0]])]})]);}
            var Q1;
            Q1=makeQuery(id+"F5.boolean.opBoolean","SPLIT",FACE,{"disambiguationData":[TD([makeQuery(id+"F5.opExtrude","SWEPT_FACE",FACE,{"disambiguationData":[OSD([sQuery(id+"F4.wireOp",EDGE,"E41")])]})])],"derivedFrom":makeQuery(id+"F3.boolean.opBoolean","COPY",FACE,{"derivedFrom":makeQuery(id+"F3.opExtrude","CAP_FACE",FACE,{"disambiguationData":[OSD([sQuery(id+"F0.wireOp",EDGE,"E25.0"),sQuery(id+"F0.wireOp",EDGE,"E25.1"),sQuery(id+"F0.wireOp",EDGE,"E25.2"),sQuery(id+"F0.wireOp",EDGE,"E25.3"),sQuery(id+"F0.wireOp",EDGE,"E25.4"),sQuery(id+"F0.wireOp",EDGE,"E25.5"),sQuery(id+"F0.wireOp",EDGE,"E25.6"),sQuery(id+"F0.wireOp",EDGE,"E25.7")])],"isStart":false})})});
            extrude(context, id + "F13", {"entities" : qUnion([Q0]), "operationType" : NewBodyOperationType.REMOVE, "endBound" : BoundingType.UP_TO_SURFACE, "endBoundEntityFace" : qUnion([Q1]), "depth" : 25 * mm});
        }
        {
            var Q0;
            Q0=makeQuery(id+"F3.boolean.opBoolean","COPY",EDGE,{"derivedFrom":makeQuery(id+"F3.opExtrude","CAP_EDGE",EDGE,{"disambiguationData":[OSD([sQuery(id+"F0.wireOp",EDGE,"E25.6")])],"isStart":false})});
            var Q1;
            Q1=makeQuery(id+"F8.boolean.opBoolean","INTERSECT",EDGE,{"derivedFrom":[makeQuery(id+"F5.opExtrude","SWEPT_FACE",FACE,{"disambiguationData":[OSD([sQuery(id+"F4.wireOp",EDGE,"E30")])]}),makeQuery(id+"F8.opExtrude","CAP_FACE",FACE,{"disambiguationData":[OSD([sQuery(id+"F7.wireOp",EDGE,"E67")])],"isStart":false})]});
            var Q2;
            Q2=makeQuery(id+"F8.boolean.opBoolean","INTERSECT",EDGE,{"disambiguationData":[OD(1.0)],"derivedFrom":[makeQuery(id+"F5.opExtrude","SWEPT_FACE",FACE,{"disambiguationData":[OSD([sQuery(id+"F4.wireOp",EDGE,"E30")])]}),makeQuery(id+"F8.opExtrude","SWEPT_FACE",FACE,{"disambiguationData":[OSD([sQuery(id+"F7.wireOp",EDGE,"E67")])]})]});
            var Q3;
            {var subQ0=sQuery(id+"F4.wireOp",EDGE,"E30");Q3=makeQuery(id+"F8.boolean.opBoolean","SPLIT",EDGE,{"disambiguationData":[TD([makeQuery(id+"F5.opExtrude","SWEPT_FACE",FACE,{"disambiguationData":[OSD([sQuery(id+"F4.wireOp",EDGE,"E35.filletArc")])]})])],"derivedFrom":makeQuery(id+"F5.opExtrude","CAP_EDGE",EDGE,{"disambiguationData":[OSD([subQ0])],"isStart":false})});}
            var Q4;
            {var subQ0=sQuery(id+"F0.wireOp",EDGE,"E25.7");var subQ1=sQuery(id+"F0.wireOp",EDGE,"E25.1");var subQ2=sQuery(id+"F0.wireOp",EDGE,"E25.6");var subQ3=sQuery(id+"F0.wireOp",EDGE,"E25.5");var subQ4=sQuery(id+"F0.wireOp",EDGE,"E25.4");var subQ5=sQuery(id+"F0.wireOp",EDGE,"E25.0");var subQ6=sQuery(id+"F0.wireOp",EDGE,"E25.2");var subQ7=sQuery(id+"F0.wireOp",EDGE,"E25.3");Q4=makeQuery(id+"F8.boolean.opBoolean","INTERSECT",EDGE,{"derivedFrom":[makeQuery(id+"F5.boolean.opBoolean","SPLIT",FACE,{"disambiguationData":[TD([makeQuery(id+"F2.opExtrude","SWEPT_FACE",FACE,{"disambiguationData":[OSD([subQ5])]})])],"derivedFrom":makeQuery(id+"F3.boolean.opBoolean","COPY",FACE,{"derivedFrom":makeQuery(id+"F3.opExtrude","CAP_FACE",FACE,{"disambiguationData":[OSD([subQ5,subQ1,subQ6,subQ7,subQ4,subQ3,subQ2,subQ0])],"isStart":false})})}),makeQuery(id+"F8.opExtrude","SWEPT_FACE",FACE,{"disambiguationData":[OSD([sQuery(id+"F7.wireOp",EDGE,"E67")])]})]});}
            var Q5;
            Q5=makeQuery(id+"F8.boolean.opBoolean","INTERSECT",EDGE,{"disambiguationData":[OD(0.0)],"derivedFrom":[makeQuery(id+"F5.opExtrude","SWEPT_FACE",FACE,{"disambiguationData":[OSD([sQuery(id+"F4.wireOp",EDGE,"E30")])]}),makeQuery(id+"F8.opExtrude","SWEPT_FACE",FACE,{"disambiguationData":[OSD([sQuery(id+"F7.wireOp",EDGE,"E67")])]})]});
            fillet(context, id + "F14", {"entities" : qUnion([Q0, Q1, Q2, Q3, Q4, Q5]), "radius" : 3 * mm, "tangentPropagation" : true, "allowEdgeOverflow" : false});
        }
        {
            var Q0;
            Q0=makeQuery(id+"F1.opExtrude","CAP_EDGE",EDGE,{"disambiguationData":[OSD([sQuery(id+"F0.wireOp",EDGE,"E1.bottom")])],"isStart":false});
            fillet(context, id + "F15", {"entities" : qUnion([Q0]), "radius" : 2 * mm, "tangentPropagation" : true, "allowEdgeOverflow" : false});
        }
        {
            var Q0;
            {var subQ0=sQuery(id+"F0.wireOp",EDGE,"E21.filletArc");var subQ1=sQuery(id+"F0.wireOp",EDGE,"E7");var subQ2=sQuery(id+"F0.wireOp",EDGE,"E6");var subQ3=sQuery(id+"F0.wireOp",EDGE,"E5");var subQ4=sQuery(id+"F0.wireOp",EDGE,"E4");var subQ5=sQuery(id+"F0.wireOp",EDGE,"E22.filletArc");var subQ6=sQuery(id+"F0.wireOp",EDGE,"E1.bottom");var subQ7=sQuery(id+"F0.wireOp",EDGE,"E1.right");var subQ8=sQuery(id+"F0.wireOp",EDGE,"E1.top");var subQ9=sQuery(id+"F0.wireOp",EDGE,"E1.left");var subQ10=sQuery(id+"F0.wireOp",EDGE,"E23.filletArc");var subQ11=sQuery(id+"F0.wireOp",EDGE,"E24.filletArc");Q0=makeQuery(id+"F2.boolean.opBoolean","SPLIT",FACE,{"disambiguationData":[TD([makeQuery(id+"F1.opExtrude","SWEPT_FACE",FACE,{"disambiguationData":[OSD([subQ6])]})])],"derivedFrom":makeQuery(id+"F1.opExtrude","CAP_FACE",FACE,{"disambiguationData":[OSD([subQ6,subQ8,subQ9,subQ7,subQ4,subQ3,subQ2,subQ1,subQ0,subQ5,subQ10,subQ11])],"isStart":true})});}
            var sketch = newSketch(context, id + "F16", { "sketchPlane" : qUnion([Q0])});
            skLineSegment(sketch, "E79", {"start": v(0, 90) * mm, "end": v(0, 120) * mm, "construction": true});
            skCircle(sketch, "E80", {"center": v(0, 120) * mm, "radius": 6 * mm});
            skLineSegment(sketch, "E81", {"start": v(15, 108) * mm, "end": v(33, 90) * mm});
            skLineSegment(sketch, "E82", {"start": v(-15, 108) * mm, "end": v(-33, 90) * mm});
            skLineSegment(sketch, "E83", {"start": v(-15, 108) * mm, "end": v(-15, 120) * mm});
            skLineSegment(sketch, "E84", {"start": v(15, 108) * mm, "end": v(15, 120) * mm});
            skArc(sketch, "E85", {"start": v(15, 120) * mm, "mid": v(0, 135) * mm, "end": v(-15, 120) * mm});
            skLineSegment(sketch, "E86", {"start": v(-80, 0) * mm, "end": v(68.5, 0) * mm, "construction": true});
            skLineSegment(sketch, "E87.MirrorCS", {"start": v(15, -108) * mm, "end": v(33, -90) * mm});
            skLineSegment(sketch, "E88.MirrorCS", {"start": v(15, -108) * mm, "end": v(15, -120) * mm});
            skArc(sketch, "E89.MirrorCS", {"start": v(15, -120) * mm, "mid": v(0, -135) * mm, "end": v(-15, -120) * mm});
            skLineSegment(sketch, "E90.MirrorCS", {"start": v(-15, -108) * mm, "end": v(-15, -120) * mm});
            skLineSegment(sketch, "E91.MirrorCS", {"start": v(-15, -108) * mm, "end": v(-33, -90) * mm});
            skLineSegment(sketch, "E92.MirrorCS", {"start": v(0, -90) * mm, "end": v(0, -120) * mm, "construction": true});
            skCircle(sketch, "E93.MirrorC", {"center": v(0, -120) * mm, "radius": 6 * mm});
            skSolve(sketch);
        }
        {
            var Q0;
            {var subQ0=sQuery(id+"F16.wireOp",EDGE,"E87.MirrorCS");Q0=makeQuery(id+"F16.imprint","IMPRINT",FACE,{"disambiguationData":[TD([[makeQuery(id+"F16.imprint","IMPRINT",EDGE,{"derivedFrom":subQ0}),1.0]])]});}
            var Q1;
            Q1=makeQuery(id+"F16.imprint","IMPRINT",FACE,{"disambiguationData":[TD([[makeQuery(id+"F16.imprint","IMPRINT",EDGE,{"derivedFrom":sQuery(id+"F16.wireOp",EDGE,"E80")}),-1.0]])]});
            var Q2;
            Q2=makeQuery(id+"F16.imprint","IMPRINT",FACE,{"disambiguationData":[TD([[makeQuery(id+"F16.imprint","IMPRINT",EDGE,{"derivedFrom":makeQuery(id+"F1.opExtrude","CAP_EDGE",EDGE,{"disambiguationData":[OSD([sQuery(id+"F0.wireOp",EDGE,"E1.left")])],"isStart":true})}),-1.0]])]});
            var Q3;
            {var subQ0=sQuery(id+"F4.wireOp",EDGE,"E36.filletArc");var subQ1=sQuery(id+"F4.wireOp",EDGE,"E35.filletArc");var subQ2=sQuery(id+"F4.wireOp",EDGE,"E34.filletArc");var subQ3=sQuery(id+"F4.wireOp",EDGE,"E33.filletArc");var subQ4=sQuery(id+"F4.wireOp",EDGE,"E27.0");var subQ5=sQuery(id+"F4.wireOp",EDGE,"E30");var subQ6=sQuery(id+"F4.wireOp",EDGE,"E28.0");var subQ7=sQuery(id+"F4.wireOp",EDGE,"E29");Q3=makeQuery(id+"F6.boolean.opBoolean","SPLIT",FACE,{"disambiguationData":[TD([makeQuery(id+"F5.opExtrude","SWEPT_FACE",FACE,{"disambiguationData":[OSD([subQ4])]})])],"derivedFrom":makeQuery(id+"F5.opExtrude","CAP_FACE",FACE,{"disambiguationData":[OSD([subQ4,subQ6,subQ7,subQ5,subQ3,subQ2,subQ1,subQ0,sQuery(id+"F4.wireOp",EDGE,"E41"),sQuery(id+"F4.wireOp",EDGE,"E42"),sQuery(id+"F4.wireOp",EDGE,"E43"),sQuery(id+"F4.wireOp",EDGE,"E45"),sQuery(id+"F4.wireOp",EDGE,"E46"),sQuery(id+"F4.wireOp",EDGE,"E47.filletArc"),sQuery(id+"F4.wireOp",EDGE,"E48.filletArc"),sQuery(id+"F4.wireOp",EDGE,"E49.filletArc"),sQuery(id+"F4.wireOp",EDGE,"E50.filletArc"),sQuery(id+"F4.wireOp",EDGE,"E51.filletArc"),sQuery(id+"F4.wireOp",EDGE,"E52.filletArc"),sQuery(id+"F4.wireOp",EDGE,"E53.0.MirrorCS"),sQuery(id+"F4.wireOp",EDGE,"E54.0.MirrorCS"),sQuery(id+"F4.wireOp",EDGE,"E55.0.MirrorCS"),sQuery(id+"F4.wireOp",EDGE,"E56.0.MirrorCS"),sQuery(id+"F4.wireOp",EDGE,"E57.0.MirrorCS"),sQuery(id+"F4.wireOp",EDGE,"E58.0.MirrorCS"),sQuery(id+"F4.wireOp",EDGE,"E59.0.MirrorCS"),sQuery(id+"F4.wireOp",EDGE,"E60.0.MirrorCS"),sQuery(id+"F4.wireOp",EDGE,"E61.0.MirrorCS"),sQuery(id+"F4.wireOp",EDGE,"E62.0.MirrorCS"),sQuery(id+"F4.wireOp",EDGE,"E63.0.MirrorCS")])],"isStart":true})});}
            extrude(context, id + "F17", {"entities" : qUnion([Q0, Q1, Q2]), "operationType" : NewBodyOperationType.ADD, "endBound" : BoundingType.UP_TO_SURFACE, "endBoundEntityFace" : qUnion([Q3]), "depth" : 25 * mm});
        }
    });
